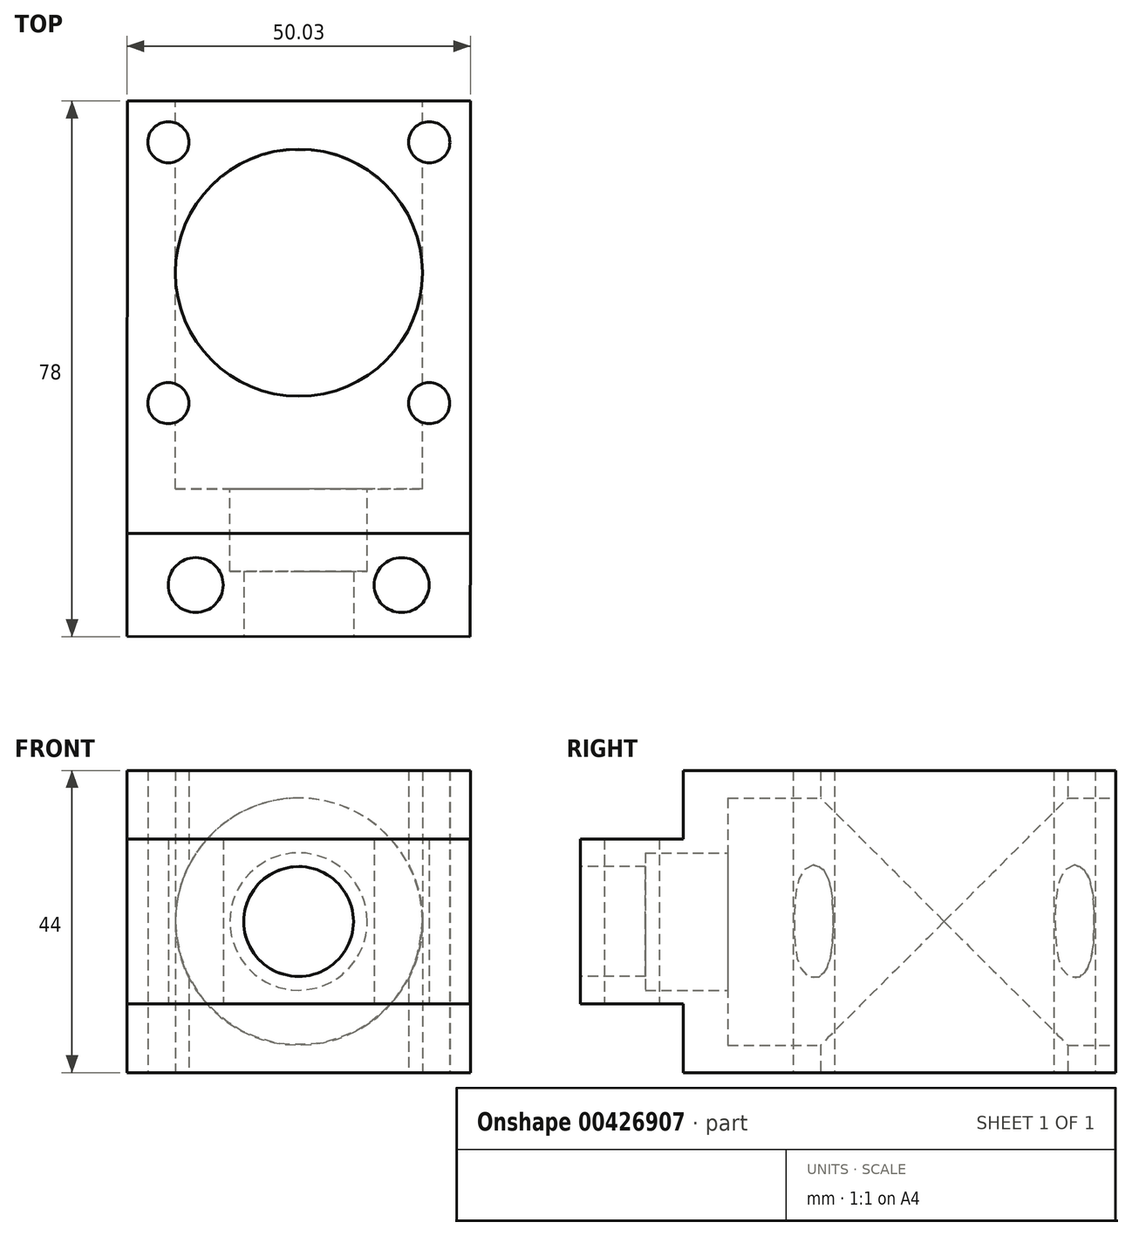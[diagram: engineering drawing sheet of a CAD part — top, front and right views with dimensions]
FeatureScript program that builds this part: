
annotation { "Feature Type Name" : "Feature", "Feature Type Description" : "" }
export const myFeature = defineFeature(function(context is Context, id is Id, definition is map)
    precondition{}
    {
        {
            var Q0;
            Q0=qCreatedBy(makeId("Top.planeOp"),FACE);
            var sketch = newSketch(context, id + "F0", { "sketchPlane" : qUnion([Q0])});
            skLineSegment(sketch, "E0", {"start": v(-49.97, 37.12) * mm, "end": v(0.03, 37.12) * mm});
            skLineSegment(sketch, "E1", {"start": v(0.03, 37.12) * mm, "end": v(0, -40.88) * mm});
            skLineSegment(sketch, "E2", {"start": v(0, -40.88) * mm, "end": v(-50, -40.86) * mm});
            skLineSegment(sketch, "E3", {"start": v(-50, -40.86) * mm, "end": v(-49.97, 37.12) * mm});
            skLineSegment(sketch, "E4.0", {"start": v(0, -25.88) * mm, "end": v(-50, -25.86) * mm});
            skCircle(sketch, "E5", {"center": v(-24.97, 12.12) * mm, "radius": 18 * mm});
            skCircle(sketch, "E6", {"center": v(-43.97, 31.12) * mm, "radius": 3 * mm});
            skCircle(sketch, "E7", {"center": v(-5.97, 31.12) * mm, "radius": 3 * mm});
            skCircle(sketch, "E8", {"center": v(-5.99, -6.88) * mm, "radius": 3 * mm});
            skCircle(sketch, "E9", {"center": v(-43.99, -6.88) * mm, "radius": 3 * mm});
            skCircle(sketch, "E10", {"center": v(-40, -33.37) * mm, "radius": 4 * mm});
            skCircle(sketch, "E11", {"center": v(-10, -33.38) * mm, "radius": 4 * mm});
            skSolve(sketch);
        }
        {
            var Q0;
            {var subQ0=sQuery(id+"F0.wireOp",EDGE,"E0");Q0=makeQuery(id+"F0.imprint","IMPRINT",FACE,{"disambiguationData":[TD([[makeQuery(id+"F0.imprint","IMPRINT",EDGE,{"derivedFrom":subQ0}),-1.0]])]});}
            extrude(context, id + "F1", {"entities" : qUnion([Q0]), "endBound" : BoundingType.SYMMETRIC, "depth" : 44 * mm});
        }
        {
            var Q0;
            {var subQ0=sQuery(id+"F0.wireOp",EDGE,"E2");Q0=makeQuery(id+"F0.imprint","IMPRINT",FACE,{"disambiguationData":[TD([[makeQuery(id+"F0.imprint","IMPRINT",EDGE,{"derivedFrom":subQ0}),-1.0]])]});}
            extrude(context, id + "F2", {"entities" : qUnion([Q0]), "operationType" : NewBodyOperationType.ADD, "endBound" : BoundingType.SYMMETRIC, "depth" : 24 * mm});
        }
        {
            var Q0;
            Q0=makeQuery(id+"F1.opExtrude","SWEPT_FACE",FACE,{"disambiguationData":[OSD([sQuery(id+"F0.wireOp",EDGE,"E0")])]});
            var sketch = newSketch(context, id + "F3", { "sketchPlane" : qUnion([Q0])});
            skLineSegment(sketch, "E12", {"start": v(-0.03, 0) * mm, "end": v(24.97, 0) * mm});
            skCircle(sketch, "E13", {"center": v(24.97, 0) * mm, "radius": 18 * mm});
            skSolve(sketch);
        }
        {
            var Q0;
            Q0=makeQuery(id+"F2.opExtrude","SWEPT_FACE",FACE,{"disambiguationData":[OSD([sQuery(id+"F0.wireOp",EDGE,"E2")])]});
            var sketch = newSketch(context, id + "F4", { "sketchPlane" : qUnion([Q0])});
            skLineSegment(sketch, "E14", {"start": v(0, 0) * mm, "end": v(-25, 0) * mm});
            skCircle(sketch, "E15", {"center": v(-25, 0) * mm, "radius": 8 * mm});
            skSolve(sketch);
        }
        {
            var Q0;
            Q0=makeQuery(id+"F4.imprint","IMPRINT",FACE,{"disambiguationData":[TD([[makeQuery(id+"F4.imprint","IMPRINT",EDGE,{"derivedFrom":sQuery(id+"F4.wireOp",EDGE,"E15")}),1.0]])]});
            extrude(context, id + "F5", {"entities" : qUnion([Q0]), "operationType" : NewBodyOperationType.REMOVE, "endBound" : BoundingType.THROUGH_ALL, "oppositeDirection" : true, "depth" : 25 * mm});
        }
        {
            var Q0;
            Q0=makeQuery(id+"F3.imprint","IMPRINT",FACE,{"disambiguationData":[TD([[makeQuery(id+"F3.imprint","IMPRINT",EDGE,{"derivedFrom":sQuery(id+"F3.wireOp",EDGE,"E13")}),1.0]])]});
            extrude(context, id + "F6", {"entities" : qUnion([Q0]), "operationType" : NewBodyOperationType.REMOVE, "oppositeDirection" : true, "depth" : 56.5 * mm});
        }
        {
            var Q0;
            Q0=makeQuery(id+"F6.boolean.opBoolean","COPY",FACE,{"derivedFrom":makeQuery(id+"F6.opExtrude","CAP_FACE",FACE,{"disambiguationData":[OSD([sQuery(id+"F3.wireOp",EDGE,"E13")])],"isStart":false})});
            var sketch = newSketch(context, id + "F7", { "sketchPlane" : qUnion([Q0])});
            skCircle(sketch, "E16", {"center": v(25, 0) * mm, "radius": 10 * mm});
            skSolve(sketch);
        }
        {
            var Q0;
            Q0=makeQuery(id+"F7.imprint","IMPRINT",FACE,{"disambiguationData":[TD([[makeQuery(id+"F7.imprint","IMPRINT",EDGE,{"derivedFrom":sQuery(id+"F7.wireOp",EDGE,"E16")}),1.0]])]});
            extrude(context, id + "F8", {"entities" : qUnion([Q0]), "operationType" : NewBodyOperationType.REMOVE, "oppositeDirection" : true, "depth" : 12 * mm});
        }
    });
